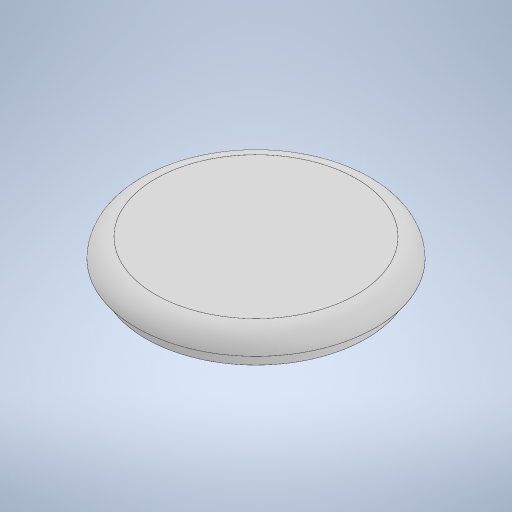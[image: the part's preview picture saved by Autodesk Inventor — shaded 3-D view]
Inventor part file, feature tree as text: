
AUTODESK INVENTOR PART (.ipt)
format: ipt  version: 2024.3 (Build 283343000, 343)  size: 275,456 bytes
history: native  units: mm
features: sketch x3, extrude x3, other x1, fillet x1, hole x1
ambient origin geometry x8: Origin, YZ Plane, XZ Plane, XY Plane, X Axis, Y Axis, Z Axis, Center Point
bodies: Body1 (feature_tree)
feature tree (9):
  other  "Sólido1"
  sketch  "Boceto1"  dims[d1=8.0mm d2=0.0mm d3=8.0mm d22=4.0mm]
  extrude  "Extrusión1"  Depth=8.0mm
  fillet  "Empalme1"  Radius=4.0mm
  extrude  "Extrusión3"  Depth=6.0mm
  sketch  "Boceto3"  dims[d26=2.459mm d27=8.0mm d28=4.0mm d29=2.0mm d30=90.0deg d31=8.8mm d32=0.0mm d33=60.0mm d35=360.0deg d37=18.0mm d38=5.0mm d39=0.0mm]
  hole  "Agujero2"  [1 undecoded]
  extrude  "Extrusión4"  Depth=5.0mm
  sketch  "Boceto2"  dims[d23=6.0mm d24=0.0mm d25=37.5mm]
note: 1 required parameter value undecoded (feature->parameter linkage not recoverable at this tier; creation-order binding heuristic only, values carry confidence <= 0.55)
